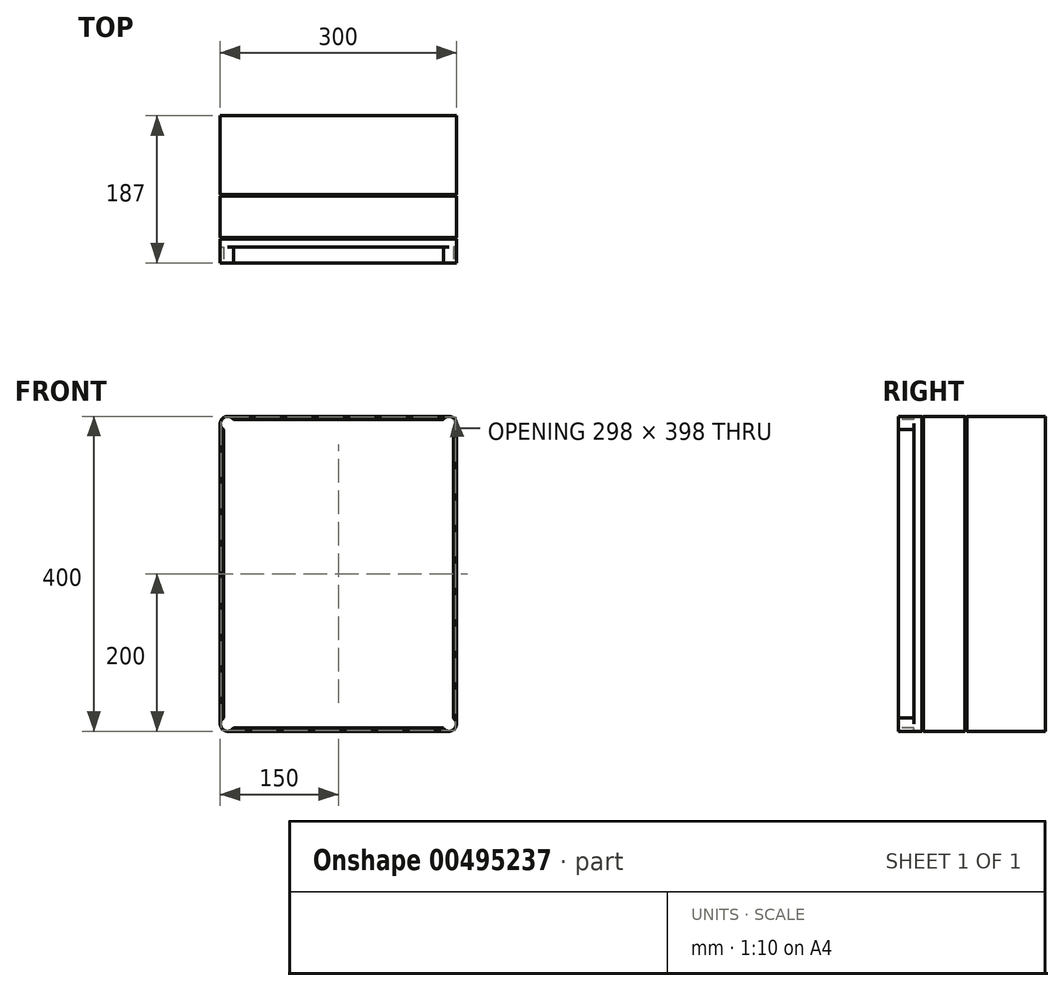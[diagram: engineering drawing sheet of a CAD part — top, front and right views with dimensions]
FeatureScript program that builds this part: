
annotation { "Feature Type Name" : "Feature", "Feature Type Description" : "" }
export const myFeature = defineFeature(function(context is Context, id is Id, definition is map)
    precondition{}
    {
        {
            var Q0;
            Q0=qCreatedBy(makeId("Front.planeOp"),FACE);
            var sketch = newSketch(context, id + "F0", { "sketchPlane" : qUnion([Q0])});
            skLineSegment(sketch, "E0.bottom", {"start": v(-140.9, 200) * mm, "end": v(140.9, 200) * mm});
            skLineSegment(sketch, "E0.top", {"start": v(-140.9, -200) * mm, "end": v(140.9, -200) * mm});
            skLineSegment(sketch, "E0.left", {"start": v(-150, 190.9) * mm, "end": v(-150, -190.9) * mm});
            skLineSegment(sketch, "E0.right", {"start": v(150, 190.9) * mm, "end": v(150, -190.9) * mm});
            skPoint(sketch, "E0.middle", {"position": v(0, 0) * mm});
            skPoint(sketch, "E1.visualSharp", {"position": v(-150, 200) * mm});
            skArc(sketch, "E1.filletArc", {"start": v(-140.9, 200) * mm, "mid": v(-147.33, 197.33) * mm, "end": v(-150, 190.9) * mm});
            skPoint(sketch, "E2.visualSharp", {"position": v(150, 200) * mm});
            skArc(sketch, "E2.filletArc", {"start": v(150, 190.9) * mm, "mid": v(147.33, 197.33) * mm, "end": v(140.9, 200) * mm});
            skPoint(sketch, "E3.visualSharp", {"position": v(-150, -200) * mm});
            skArc(sketch, "E3.filletArc", {"start": v(-150, -190.9) * mm, "mid": v(-147.33, -197.33) * mm, "end": v(-140.9, -200) * mm});
            skPoint(sketch, "E4.visualSharp", {"position": v(150, -200) * mm});
            skArc(sketch, "E4.filletArc", {"start": v(140.9, -200) * mm, "mid": v(147.33, -197.33) * mm, "end": v(150, -190.9) * mm});
            skSolve(sketch);
        }
        {
            var Q0;
            Q0=qSketchRegion(id+"F0",true);
            extrude(context, id + "F1", {"entities" : qUnion([Q0]), "depth" : 100 * mm});
        }
        {
            var Q0;
            Q0=makeQuery(id+"F1.opExtrude","CAP_FACE",FACE,{"disambiguationData":[OSD([sQuery(id+"F0.wireOp",EDGE,"E0.bottom"),sQuery(id+"F0.wireOp",EDGE,"E0.top"),sQuery(id+"F0.wireOp",EDGE,"E0.left"),sQuery(id+"F0.wireOp",EDGE,"E0.right")])],"isStart":false});
            var sketch = newSketch(context, id + "F2", { "sketchPlane" : qUnion([Q0])});
            skLineSegment(sketch, "E5.0.0", {"start": v(-150, 190.9) * mm, "end": v(-150, -190.9) * mm});
            skLineSegment(sketch, "E5.0.1", {"start": v(-140.9, -200) * mm, "end": v(-140.9, -200) * mm});
            skLineSegment(sketch, "E5.0.2", {"start": v(150, -190.9) * mm, "end": v(150, 190.9) * mm});
            skLineSegment(sketch, "E5.0.3", {"start": v(140.9, 200) * mm, "end": v(-140.9, 200) * mm});
            skLineSegment(sketch, "E6.0", {"start": v(139.9, 199) * mm, "end": v(-139.9, 199) * mm});
            skLineSegment(sketch, "E6.1", {"start": v(149, -189.9) * mm, "end": v(149, 189.9) * mm});
            skLineSegment(sketch, "E6.2", {"start": v(-139.9, -199) * mm, "end": v(139.9, -199) * mm});
            skLineSegment(sketch, "E6.3", {"start": v(-149, 189.9) * mm, "end": v(-149, -189.9) * mm});
            skPoint(sketch, "E7.visualSharp", {"position": v(-149, 199) * mm});
            skArc(sketch, "E7.filletArc", {"start": v(-139.9, 199) * mm, "mid": v(-146.33, 196.33) * mm, "end": v(-149, 189.9) * mm});
            skPoint(sketch, "E8.newPointB", {"position": v(-150, 190.9) * mm});
            skArc(sketch, "E8.filletArc", {"start": v(-140.9, 200) * mm, "mid": v(-147.33, 197.33) * mm, "end": v(-150, 190.9) * mm});
            skPoint(sketch, "E9.visualSharp", {"position": v(149, 199) * mm});
            skArc(sketch, "E9.filletArc", {"start": v(149, 189.9) * mm, "mid": v(146.33, 196.33) * mm, "end": v(139.9, 199) * mm});
            skPoint(sketch, "E10.newPointA", {"position": v(150, 190.9) * mm});
            skArc(sketch, "E10.filletArc", {"start": v(150, 190.9) * mm, "mid": v(147.33, 197.33) * mm, "end": v(140.9, 200) * mm});
            skPoint(sketch, "E11.visualSharp", {"position": v(149, -199) * mm});
            skArc(sketch, "E11.filletArc", {"start": v(139.9, -199) * mm, "mid": v(146.33, -196.33) * mm, "end": v(149, -189.9) * mm});
            skPoint(sketch, "E12.visualSharp", {"position": v(-149, -199) * mm});
            skArc(sketch, "E12.filletArc", {"start": v(-149, -189.9) * mm, "mid": v(-146.33, -196.33) * mm, "end": v(-139.9, -199) * mm});
            skPoint(sketch, "E13.newPointA", {"position": v(-150, -190.9) * mm});
            skArc(sketch, "E13.filletArc", {"start": v(-150, -190.9) * mm, "mid": v(-147.33, -197.33) * mm, "end": v(-140.9, -200) * mm});
            skLineSegment(sketch, "E14.0", {"start": v(-140.9, -200) * mm, "end": v(140.9, -200) * mm});
            skPoint(sketch, "E15.newPointA", {"position": v(140.9, -200) * mm});
            skArc(sketch, "E15.filletArc", {"start": v(140.9, -200) * mm, "mid": v(147.33, -197.33) * mm, "end": v(150, -190.9) * mm});
            skSolve(sketch);
        }
        {
            var Q0;
            Q0=makeQuery(id+"F2.imprint","IMPRINT",FACE,{"disambiguationData":[TD([[makeQuery(id+"F2.imprint","IMPRINT",EDGE,{"derivedFrom":sQuery(id+"F2.wireOp",EDGE,"E6.0")}),1.0]])]});
            extrude(context, id + "F3", {"entities" : qUnion([Q0]), "operationType" : NewBodyOperationType.ADD, "depth" : 2 * mm});
        }
        {
            var Q0;
            Q0=makeQuery(id+"F3.opExtrude","CAP_FACE",FACE,{"disambiguationData":[OSD([sQuery(id+"F2.wireOp",EDGE,"E6.0"),sQuery(id+"F2.wireOp",EDGE,"E6.1"),sQuery(id+"F2.wireOp",EDGE,"E6.2"),sQuery(id+"F2.wireOp",EDGE,"E6.3")])],"isStart":false});
            var sketch = newSketch(context, id + "F4", { "sketchPlane" : qUnion([Q0])});
            skArc(sketch, "E16.0.0", {"start": v(-150, -190.9) * mm, "mid": v(-147.33, -197.33) * mm, "end": v(-140.9, -200) * mm});
            skLineSegment(sketch, "E16.0.1", {"start": v(-140.9, -200) * mm, "end": v(140.9, -200) * mm});
            skArc(sketch, "E16.0.2", {"start": v(140.9, -200) * mm, "mid": v(147.33, -197.33) * mm, "end": v(150, -190.9) * mm});
            skLineSegment(sketch, "E16.0.3", {"start": v(150, -190.9) * mm, "end": v(150, 190.9) * mm});
            skArc(sketch, "E16.0.4", {"start": v(150, 190.9) * mm, "mid": v(147.33, 197.33) * mm, "end": v(140.9, 200) * mm});
            skLineSegment(sketch, "E16.0.5", {"start": v(140.9, 200) * mm, "end": v(-140.9, 200) * mm});
            skArc(sketch, "E16.0.6", {"start": v(-140.9, 200) * mm, "mid": v(-147.33, 197.33) * mm, "end": v(-150, 190.9) * mm});
            skLineSegment(sketch, "E16.0.7", {"start": v(-150, 190.9) * mm, "end": v(-150, -190.9) * mm});
            skSolve(sketch);
        }
        {
            var Q0;
            Q0=makeQuery(id+"F4.imprint","IMPRINT",FACE,{"disambiguationData":[TD([[makeQuery(id+"F4.imprint","IMPRINT",EDGE,{"derivedFrom":sQuery(id+"F4.wireOp",EDGE,"E16.0.0")}),1.0]])]});
            var Q1;
            Q1=makeQuery(id+"F4.imprint","IMPRINT",FACE,{"disambiguationData":[TD([[makeQuery(id+"F4.imprint","IMPRINT",EDGE,{"derivedFrom":makeQuery(id+"F3.opExtrude","CAP_EDGE",EDGE,{"disambiguationData":[OSD([sQuery(id+"F2.wireOp",EDGE,"E6.0")])],"isStart":false})}),1.0]])]});
            extrude(context, id + "F5", {"entities" : qUnion([Q0, Q1]), "depth" : 53 * mm});
        }
        {
            var Q0;
            Q0=makeQuery(id+"F5.opExtrude","CAP_FACE",FACE,{"disambiguationData":[OSD([sQuery(id+"F4.wireOp",EDGE,"E16.0.0"),sQuery(id+"F4.wireOp",EDGE,"E16.0.1"),sQuery(id+"F4.wireOp",EDGE,"E16.0.2"),sQuery(id+"F4.wireOp",EDGE,"E16.0.3"),sQuery(id+"F4.wireOp",EDGE,"E16.0.4"),sQuery(id+"F4.wireOp",EDGE,"E16.0.5"),sQuery(id+"F4.wireOp",EDGE,"E16.0.6"),sQuery(id+"F4.wireOp",EDGE,"E16.0.7")])],"isStart":false});
            var sketch = newSketch(context, id + "F6", { "sketchPlane" : qUnion([Q0])});
            skArc(sketch, "E17.0", {"start": v(-139.9, 199) * mm, "mid": v(-146.33, 196.33) * mm, "end": v(-149, 189.9) * mm});
            skLineSegment(sketch, "E17.1", {"start": v(139.9, 199) * mm, "end": v(-139.9, 199) * mm});
            skLineSegment(sketch, "E17.2", {"start": v(-149, 189.9) * mm, "end": v(-149, -189.9) * mm});
            skArc(sketch, "E17.3", {"start": v(149, 189.9) * mm, "mid": v(146.33, 196.33) * mm, "end": v(139.9, 199) * mm});
            skLineSegment(sketch, "E17.4", {"start": v(149, -189.9) * mm, "end": v(149, 189.9) * mm});
            skArc(sketch, "E17.5", {"start": v(-149, -189.9) * mm, "mid": v(-146.33, -196.33) * mm, "end": v(-139.9, -199) * mm});
            skLineSegment(sketch, "E17.6", {"start": v(-139.9, -199) * mm, "end": v(139.9, -199) * mm});
            skArc(sketch, "E17.7", {"start": v(139.9, -199) * mm, "mid": v(146.33, -196.33) * mm, "end": v(149, -189.9) * mm});
            skSolve(sketch);
        }
        {
            var Q0;
            Q0=makeQuery(id+"F6.imprint","IMPRINT",FACE,{"disambiguationData":[TD([[makeQuery(id+"F6.imprint","IMPRINT",EDGE,{"derivedFrom":sQuery(id+"F6.wireOp",EDGE,"E17.0")}),1.0]])]});
            extrude(context, id + "F7", {"entities" : qUnion([Q0]), "operationType" : NewBodyOperationType.ADD, "depth" : 2 * mm});
        }
        {
            var Q0;
            Q0=makeQuery(id+"F7.opExtrude","CAP_FACE",FACE,{"disambiguationData":[OSD([sQuery(id+"F6.wireOp",EDGE,"E17.0"),sQuery(id+"F6.wireOp",EDGE,"E17.1"),sQuery(id+"F6.wireOp",EDGE,"E17.2"),sQuery(id+"F6.wireOp",EDGE,"E17.3"),sQuery(id+"F6.wireOp",EDGE,"E17.4"),sQuery(id+"F6.wireOp",EDGE,"E17.5"),sQuery(id+"F6.wireOp",EDGE,"E17.6"),sQuery(id+"F6.wireOp",EDGE,"E17.7")])],"isStart":false});
            var sketch = newSketch(context, id + "F8", { "sketchPlane" : qUnion([Q0])});
            skLineSegment(sketch, "E18.bottom", {"start": v(145, 195) * mm, "end": v(-145, 195) * mm});
            skLineSegment(sketch, "E18.top", {"start": v(145, -195) * mm, "end": v(-145, -195) * mm});
            skLineSegment(sketch, "E18.left", {"start": v(145, 195) * mm, "end": v(145, -195) * mm});
            skLineSegment(sketch, "E18.right", {"start": v(-145, 195) * mm, "end": v(-145, -195) * mm});
            skPoint(sketch, "E18.middle", {"position": v(0, 0) * mm});
            skArc(sketch, "E19.0.0", {"start": v(-140.9, 200) * mm, "mid": v(-147.33, 197.33) * mm, "end": v(-150, 190.9) * mm});
            skLineSegment(sketch, "E19.0.1", {"start": v(-150, 190.9) * mm, "end": v(-150, -190.9) * mm});
            skArc(sketch, "E19.0.2", {"start": v(-150, -190.9) * mm, "mid": v(-147.33, -197.33) * mm, "end": v(-140.9, -200) * mm});
            skLineSegment(sketch, "E19.0.3", {"start": v(-140.9, -200) * mm, "end": v(140.9, -200) * mm});
            skArc(sketch, "E19.0.4", {"start": v(140.9, -200) * mm, "mid": v(147.33, -197.33) * mm, "end": v(150, -190.9) * mm});
            skLineSegment(sketch, "E19.0.5", {"start": v(150, -190.9) * mm, "end": v(150, 190.9) * mm});
            skArc(sketch, "E19.0.6", {"start": v(150, 190.9) * mm, "mid": v(147.33, 197.33) * mm, "end": v(140.9, 200) * mm});
            skLineSegment(sketch, "E19.0.7", {"start": v(140.9, 200) * mm, "end": v(-140.9, 200) * mm});
            skSolve(sketch);
        }
        {
            var Q0;
            Q0=makeQuery(id+"F8.imprint","IMPRINT",FACE,{"disambiguationData":[TD([[makeQuery(id+"F8.imprint","IMPRINT",EDGE,{"derivedFrom":sQuery(id+"F8.wireOp",EDGE,"E19.0.0")}),1.0]])]});
            var Q1;
            Q1=makeQuery(id+"F8.imprint","IMPRINT",FACE,{"disambiguationData":[TD([[makeQuery(id+"F8.imprint","IMPRINT",EDGE,{"derivedFrom":sQuery(id+"F8.wireOp",EDGE,"E18.bottom")}),-1.0]])]});
            var Q2;
            Q2=makeQuery(id+"F8.imprint","IMPRINT",FACE,{"disambiguationData":[TD([[makeQuery(id+"F8.imprint","IMPRINT",EDGE,{"derivedFrom":sQuery(id+"F8.wireOp",EDGE,"E18.bottom")}),1.0]])]});
            extrude(context, id + "F9", {"entities" : qUnion([Q0, Q1, Q2]), "depth" : 30 * mm});
        }
        {
            var Q0;
            Q0=makeQuery(id+"F9.opExtrude","CAP_FACE",FACE,{"disambiguationData":[OSD([sQuery(id+"F8.wireOp",EDGE,"E19.0.0"),sQuery(id+"F8.wireOp",EDGE,"E19.0.1"),sQuery(id+"F8.wireOp",EDGE,"E19.0.2"),sQuery(id+"F8.wireOp",EDGE,"E19.0.3"),sQuery(id+"F8.wireOp",EDGE,"E19.0.4"),sQuery(id+"F8.wireOp",EDGE,"E19.0.5"),sQuery(id+"F8.wireOp",EDGE,"E19.0.6"),sQuery(id+"F8.wireOp",EDGE,"E19.0.7")])],"isStart":false});
            var sketch = newSketch(context, id + "F10", { "sketchPlane" : qUnion([Q0])});
            skArc(sketch, "E20.0.0", {"start": v(150, 190.9) * mm, "mid": v(147.33, 197.33) * mm, "end": v(140.9, 200) * mm, "construction": true});
            skLineSegment(sketch, "E20.0.1", {"start": v(140.9, 200) * mm, "end": v(-140.9, 200) * mm, "construction": true});
            skArc(sketch, "E20.0.2", {"start": v(-140.9, 200) * mm, "mid": v(-147.33, 197.33) * mm, "end": v(-150, 190.9) * mm, "construction": true});
            skLineSegment(sketch, "E20.0.3", {"start": v(-150, 190.9) * mm, "end": v(-150, -190.9) * mm, "construction": true});
            skArc(sketch, "E20.0.4", {"start": v(-150, -190.9) * mm, "mid": v(-147.33, -197.33) * mm, "end": v(-140.9, -200) * mm, "construction": true});
            skLineSegment(sketch, "E20.0.5", {"start": v(-140.9, -200) * mm, "end": v(140.9, -200) * mm, "construction": true});
            skArc(sketch, "E20.0.6", {"start": v(140.9, -200) * mm, "mid": v(147.33, -197.33) * mm, "end": v(150, -190.9) * mm, "construction": true});
            skLineSegment(sketch, "E20.0.7", {"start": v(150, -190.9) * mm, "end": v(150, 190.9) * mm, "construction": true});
            skLineSegment(sketch, "E21.bottom", {"start": v(-133, 200) * mm, "end": v(133, 200) * mm});
            skLineSegment(sketch, "E21.top", {"start": v(-133.36, 196) * mm, "end": v(133.36, 196) * mm});
            skPoint(sketch, "E22.middle", {"position": v(0, 0) * mm});
            skCircle(sketch, "E23", {"center": v(-140.9, 190.9) * mm, "radius": 9.1 * mm});
            skCircle(sketch, "E24", {"center": v(140.9, 190.9) * mm, "radius": 9.1 * mm});
            skCircle(sketch, "E25.MirrorC", {"center": v(-140.9, -190.9) * mm, "radius": 9.1 * mm});
            skLineSegment(sketch, "E26.MirrorCS", {"start": v(-133.36, -196) * mm, "end": v(133.36, -196) * mm});
            skCircle(sketch, "E27.MirrorC", {"center": v(140.9, -190.9) * mm, "radius": 9.1 * mm});
            skLineSegment(sketch, "E28.0", {"start": v(-146, 183.36) * mm, "end": v(-146, -183.36) * mm});
            skLineSegment(sketch, "E29.0", {"start": v(146, -183.36) * mm, "end": v(146, 183.36) * mm});
            skSolve(sketch);
        }
        {
            var Q0;
            {var subQ6=sQuery(id+"F10.wireOp",EDGE,"E21.bottom");Q0=makeQuery(id+"F10.imprint","IMPRINT",FACE,{"disambiguationData":[TD([[makeQuery(id+"F10.imprint","IMPRINT",EDGE,{"derivedFrom":subQ6}),1.0]])]});}
            var Q1;
            {var subQ2=sQuery(id+"F10.wireOp",EDGE,"E28.0");Q1=makeQuery(id+"F10.imprint","IMPRINT",FACE,{"disambiguationData":[TD([[makeQuery(id+"F10.imprint","IMPRINT",EDGE,{"derivedFrom":subQ2}),-1.0]])]});}
            var Q2;
            {var subQ2=sQuery(id+"F10.wireOp",EDGE,"E29.0");Q2=makeQuery(id+"F10.imprint","IMPRINT",FACE,{"disambiguationData":[TD([[makeQuery(id+"F10.imprint","IMPRINT",EDGE,{"derivedFrom":subQ2}),-1.0]])]});}
            var Q3;
            {var subQ2=sQuery(id+"F10.wireOp",EDGE,"E26.MirrorCS");Q3=makeQuery(id+"F10.imprint","IMPRINT",FACE,{"disambiguationData":[TD([[makeQuery(id+"F10.imprint","IMPRINT",EDGE,{"derivedFrom":subQ2}),-1.0]])]});}
            extrude(context, id + "F11", {"entities" : qUnion([Q0, Q1, Q2, Q3]), "operationType" : NewBodyOperationType.REMOVE, "oppositeDirection" : true, "depth" : 20 * mm});
        }
    });
